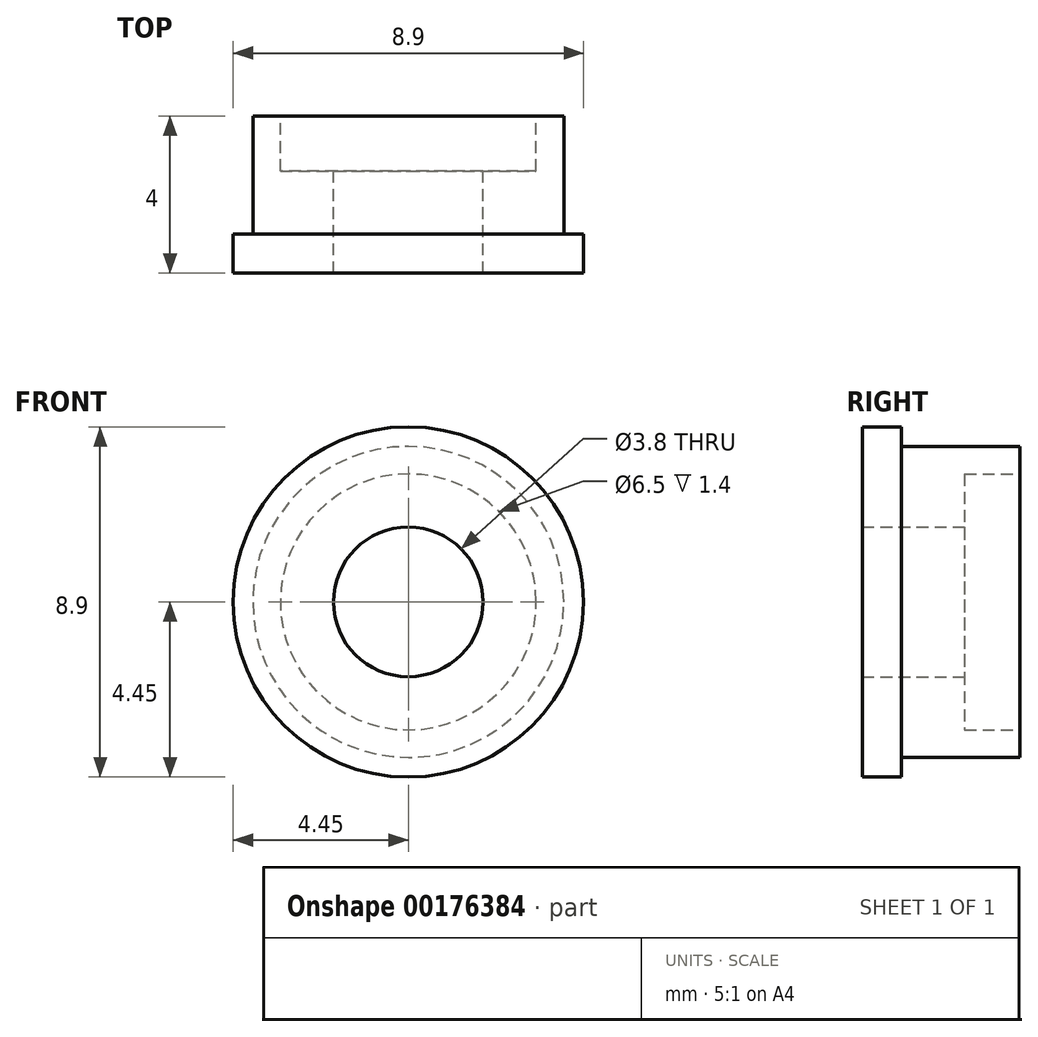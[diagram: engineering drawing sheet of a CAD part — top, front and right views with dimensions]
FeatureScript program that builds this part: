
annotation { "Feature Type Name" : "Feature", "Feature Type Description" : "" }
export const myFeature = defineFeature(function(context is Context, id is Id, definition is map)
    precondition{}
    {
        {
            var Q0;
            Q0=qCreatedBy(makeId("Right.planeOp"),FACE);
            var sketch = newSketch(context, id + "F0", { "sketchPlane" : qUnion([Q0])});
            skLineSegment(sketch, "E0", {"start": v(11.47, 0) * mm, "end": v(0, 0) * mm, "construction": true});
            skLineSegment(sketch, "E1", {"start": v(2.6, 1.9) * mm, "end": v(0, 1.9) * mm});
            skLineSegment(sketch, "E2", {"start": v(2.6, 1.9) * mm, "end": v(2.6, 3.25) * mm});
            skLineSegment(sketch, "E3", {"start": v(4, 3.25) * mm, "end": v(2.6, 3.25) * mm});
            skLineSegment(sketch, "E4", {"start": v(4, 3.25) * mm, "end": v(4, 3.95) * mm});
            skLineSegment(sketch, "E5", {"start": v(1, 3.95) * mm, "end": v(4, 3.95) * mm});
            skLineSegment(sketch, "E6", {"start": v(1, 3.95) * mm, "end": v(1, 4.45) * mm});
            skLineSegment(sketch, "E7", {"start": v(0, 4.45) * mm, "end": v(1, 4.45) * mm});
            skLineSegment(sketch, "E8", {"start": v(0, 4.45) * mm, "end": v(0, 1.9) * mm});
            skSolve(sketch);
        }
        {
            var Q0;
            Q0=makeQuery(id+"F0.imprint","IMPRINT",FACE,{"disambiguationData":[TD([[makeQuery(id+"F0.imprint","IMPRINT",EDGE,{"derivedFrom":sQuery(id+"F0.wireOp",EDGE,"E1")}),-1.0]])]});
            var Q1;
            Q1=sQuery(id+"F0.wireOp",EDGE,"E0");
            revolve(context, id + "F1", {"entities" : qUnion([Q0]), "axis" : qUnion([Q1]), "revolveType" : RevolveType.FULL});
        }
    });
